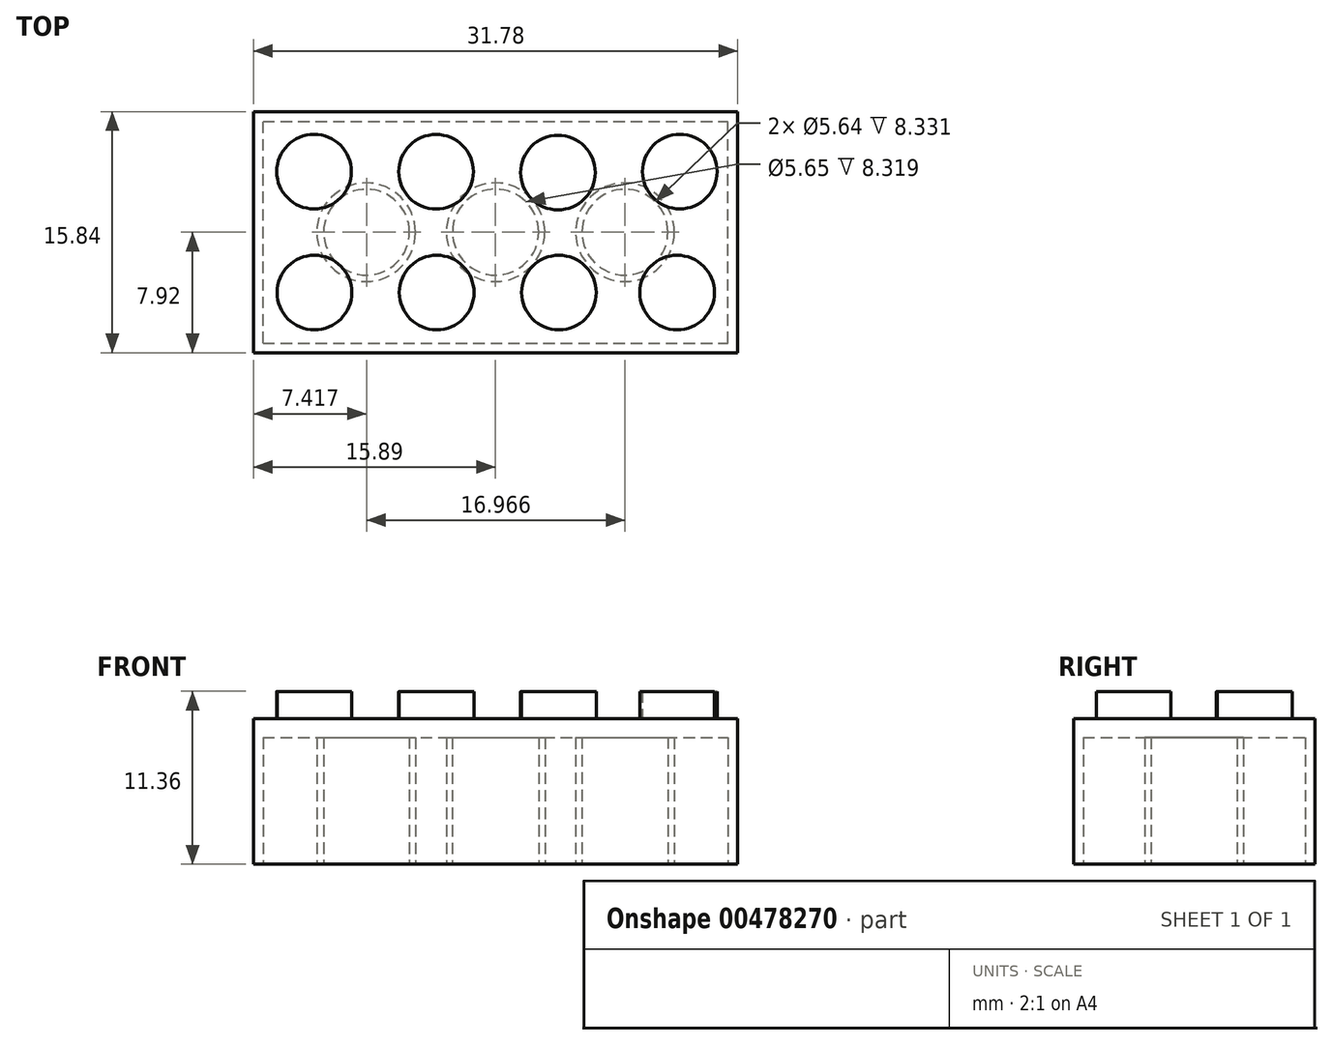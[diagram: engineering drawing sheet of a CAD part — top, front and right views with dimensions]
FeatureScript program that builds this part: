
annotation { "Feature Type Name" : "Feature", "Feature Type Description" : "" }
export const myFeature = defineFeature(function(context is Context, id is Id, definition is map)
    precondition{}
    {
        {
            var Q0;
            Q0=qCreatedBy(makeId("Top.planeOp"),FACE);
            var sketch = newSketch(context, id + "F0", { "sketchPlane" : qUnion([Q0])});
            skLineSegment(sketch, "E0.bottom", {"start": v(-15.9, 7.92) * mm, "end": v(15.9, 7.92) * mm});
            skLineSegment(sketch, "E0.top", {"start": v(-15.9, -7.92) * mm, "end": v(15.9, -7.92) * mm});
            skLineSegment(sketch, "E0.left", {"start": v(-15.9, 7.92) * mm, "end": v(-15.9, -7.92) * mm});
            skLineSegment(sketch, "E0.right", {"start": v(15.9, 7.92) * mm, "end": v(15.9, -7.92) * mm});
            skPoint(sketch, "E0.middle", {"position": v(0, 0) * mm});
            skSolve(sketch);
        }
        {
            var Q0;
            Q0=makeQuery(id+"F0.imprint","IMPRINT",FACE,{"disambiguationData":[TD([[makeQuery(id+"F0.imprint","IMPRINT",EDGE,{"derivedFrom":sQuery(id+"F0.wireOp",EDGE,"E0.bottom")}),-1.0]])]});
            extrude(context, id + "F1", {"entities" : qUnion([Q0]), "endBound" : BoundingType.SYMMETRIC, "depth" : 9.58 * mm, "offsetDistance" : 25.4 * mm});
        }
        {
            var Q0;
            Q0=makeQuery(id+"F1.opExtrude","CAP_FACE",FACE,{"disambiguationData":[OSD([sQuery(id+"F0.wireOp",EDGE,"E0.bottom"),sQuery(id+"F0.wireOp",EDGE,"E0.top"),sQuery(id+"F0.wireOp",EDGE,"E0.left"),sQuery(id+"F0.wireOp",EDGE,"E0.right")])],"isStart":false});
            var sketch = newSketch(context, id + "F2", { "sketchPlane" : qUnion([Q0])});
            skCircle(sketch, "E1", {"center": v(-11.92, 3.98) * mm, "radius": 2.45 * mm});
            skCircle(sketch, "E2", {"center": v(-11.92, -3.98) * mm, "radius": 2.45 * mm});
            skSolve(sketch);
        }
        {
            var Q0;
            Q0=makeQuery(id+"F2.imprint","IMPRINT",FACE,{"disambiguationData":[TD([[makeQuery(id+"F2.imprint","IMPRINT",EDGE,{"derivedFrom":sQuery(id+"F2.wireOp",EDGE,"E1")}),1.0]])]});
            extrude(context, id + "F3", {"entities" : qUnion([Q0]), "operationType" : NewBodyOperationType.ADD, "depth" : 1.78 * mm});
        }
        {
            var Q0;
            Q0=makeQuery(id+"F1.opExtrude","CAP_FACE",FACE,{"disambiguationData":[OSD([sQuery(id+"F0.wireOp",EDGE,"E0.bottom"),sQuery(id+"F0.wireOp",EDGE,"E0.top"),sQuery(id+"F0.wireOp",EDGE,"E0.left"),sQuery(id+"F0.wireOp",EDGE,"E0.right")])],"isStart":false});
            var sketch = newSketch(context, id + "F4", { "sketchPlane" : qUnion([Q0])});
            skCircle(sketch, "E3", {"center": v(-3.9, 3.97) * mm, "radius": 2.45 * mm});
            skSolve(sketch);
        }
        {
            var Q0;
            Q0=makeQuery(id+"F4.imprint","IMPRINT",FACE,{"disambiguationData":[TD([[makeQuery(id+"F4.imprint","IMPRINT",EDGE,{"derivedFrom":sQuery(id+"F4.wireOp",EDGE,"E3")}),1.0]])]});
            extrude(context, id + "F5", {"entities" : qUnion([Q0]), "operationType" : NewBodyOperationType.ADD, "depth" : 1.78 * mm});
        }
        {
            var Q0;
            Q0=makeQuery(id+"F1.opExtrude","CAP_FACE",FACE,{"disambiguationData":[OSD([sQuery(id+"F0.wireOp",EDGE,"E0.bottom"),sQuery(id+"F0.wireOp",EDGE,"E0.top"),sQuery(id+"F0.wireOp",EDGE,"E0.left"),sQuery(id+"F0.wireOp",EDGE,"E0.right")])],"isStart":false});
            var sketch = newSketch(context, id + "F6", { "sketchPlane" : qUnion([Q0])});
            skCircle(sketch, "E4", {"center": v(4.1, 3.92) * mm, "radius": 2.45 * mm});
            skSolve(sketch);
        }
        {
            var Q0;
            Q0=makeQuery(id+"F6.imprint","IMPRINT",FACE,{"disambiguationData":[TD([[makeQuery(id+"F6.imprint","IMPRINT",EDGE,{"derivedFrom":sQuery(id+"F6.wireOp",EDGE,"E4")}),1.0]])]});
            extrude(context, id + "F7", {"entities" : qUnion([Q0]), "operationType" : NewBodyOperationType.ADD, "depth" : 1.78 * mm});
        }
        {
            var Q0;
            Q0=makeQuery(id+"F1.opExtrude","CAP_FACE",FACE,{"disambiguationData":[OSD([sQuery(id+"F0.wireOp",EDGE,"E0.bottom"),sQuery(id+"F0.wireOp",EDGE,"E0.top"),sQuery(id+"F0.wireOp",EDGE,"E0.left"),sQuery(id+"F0.wireOp",EDGE,"E0.right")])],"isStart":false});
            var sketch = newSketch(context, id + "F8", { "sketchPlane" : qUnion([Q0])});
            skCircle(sketch, "E5", {"center": v(12.1, 3.98) * mm, "radius": 2.45 * mm});
            skSolve(sketch);
        }
        {
            var Q0;
            Q0=makeQuery(id+"F8.imprint","IMPRINT",FACE,{"disambiguationData":[TD([[makeQuery(id+"F8.imprint","IMPRINT",EDGE,{"derivedFrom":sQuery(id+"F8.wireOp",EDGE,"E5")}),1.0]])]});
            extrude(context, id + "F9", {"entities" : qUnion([Q0]), "operationType" : NewBodyOperationType.ADD, "depth" : 1.78 * mm});
        }
        {
            var Q0;
            Q0=makeQuery(id+"F1.opExtrude","CAP_FACE",FACE,{"disambiguationData":[OSD([sQuery(id+"F0.wireOp",EDGE,"E0.bottom"),sQuery(id+"F0.wireOp",EDGE,"E0.top"),sQuery(id+"F0.wireOp",EDGE,"E0.left"),sQuery(id+"F0.wireOp",EDGE,"E0.right")])],"isStart":false});
            var sketch = newSketch(context, id + "F10", { "sketchPlane" : qUnion([Q0])});
            skCircle(sketch, "E6", {"center": v(-11.9, -3.97) * mm, "radius": 2.45 * mm});
            skSolve(sketch);
        }
        {
            var Q0;
            Q0=makeQuery(id+"F10.imprint","IMPRINT",FACE,{"disambiguationData":[TD([[makeQuery(id+"F10.imprint","IMPRINT",EDGE,{"derivedFrom":sQuery(id+"F10.wireOp",EDGE,"E6")}),1.0]])]});
            extrude(context, id + "F11", {"entities" : qUnion([Q0]), "operationType" : NewBodyOperationType.ADD, "depth" : 1.78 * mm});
        }
        {
            var Q0;
            Q0=makeQuery(id+"F1.opExtrude","CAP_FACE",FACE,{"disambiguationData":[OSD([sQuery(id+"F0.wireOp",EDGE,"E0.bottom"),sQuery(id+"F0.wireOp",EDGE,"E0.top"),sQuery(id+"F0.wireOp",EDGE,"E0.left"),sQuery(id+"F0.wireOp",EDGE,"E0.right")])],"isStart":false});
            var sketch = newSketch(context, id + "F12", { "sketchPlane" : qUnion([Q0])});
            skCircle(sketch, "E7", {"center": v(-3.87, -3.97) * mm, "radius": 2.45 * mm});
            skSolve(sketch);
        }
        {
            var Q0;
            Q0=makeQuery(id+"F12.imprint","IMPRINT",FACE,{"disambiguationData":[TD([[makeQuery(id+"F12.imprint","IMPRINT",EDGE,{"derivedFrom":sQuery(id+"F12.wireOp",EDGE,"E7")}),1.0]])]});
            extrude(context, id + "F13", {"entities" : qUnion([Q0]), "operationType" : NewBodyOperationType.ADD, "depth" : 1.78 * mm});
        }
        {
            var Q0;
            Q0=makeQuery(id+"F1.opExtrude","CAP_FACE",FACE,{"disambiguationData":[OSD([sQuery(id+"F0.wireOp",EDGE,"E0.bottom"),sQuery(id+"F0.wireOp",EDGE,"E0.top"),sQuery(id+"F0.wireOp",EDGE,"E0.left"),sQuery(id+"F0.wireOp",EDGE,"E0.right")])],"isStart":false});
            var sketch = newSketch(context, id + "F14", { "sketchPlane" : qUnion([Q0])});
            skCircle(sketch, "E8", {"center": v(4.16, -3.97) * mm, "radius": 2.45 * mm});
            skSolve(sketch);
        }
        {
            var Q0;
            Q0=makeQuery(id+"F14.imprint","IMPRINT",FACE,{"disambiguationData":[TD([[makeQuery(id+"F14.imprint","IMPRINT",EDGE,{"derivedFrom":sQuery(id+"F14.wireOp",EDGE,"E8")}),1.0]])]});
            extrude(context, id + "F15", {"entities" : qUnion([Q0]), "operationType" : NewBodyOperationType.ADD, "depth" : 1.78 * mm});
        }
        {
            var Q0;
            Q0=makeQuery(id+"F1.opExtrude","CAP_FACE",FACE,{"disambiguationData":[OSD([sQuery(id+"F0.wireOp",EDGE,"E0.bottom"),sQuery(id+"F0.wireOp",EDGE,"E0.top"),sQuery(id+"F0.wireOp",EDGE,"E0.left"),sQuery(id+"F0.wireOp",EDGE,"E0.right")])],"isStart":false});
            var sketch = newSketch(context, id + "F16", { "sketchPlane" : qUnion([Q0])});
            skCircle(sketch, "E9", {"center": v(11.92, -3.97) * mm, "radius": 2.45 * mm});
            skSolve(sketch);
        }
        {
            var Q0;
            Q0=makeQuery(id+"F16.imprint","IMPRINT",FACE,{"disambiguationData":[TD([[makeQuery(id+"F16.imprint","IMPRINT",EDGE,{"derivedFrom":sQuery(id+"F16.wireOp",EDGE,"E9")}),1.0]])]});
            extrude(context, id + "F17", {"entities" : qUnion([Q0]), "operationType" : NewBodyOperationType.ADD, "depth" : 1.78 * mm});
        }
        {
            var Q0;
            Q0=makeQuery(id+"F1.opExtrude","CAP_FACE",FACE,{"disambiguationData":[OSD([sQuery(id+"F0.wireOp",EDGE,"E0.bottom"),sQuery(id+"F0.wireOp",EDGE,"E0.top"),sQuery(id+"F0.wireOp",EDGE,"E0.left"),sQuery(id+"F0.wireOp",EDGE,"E0.right")])],"isStart":true});
            var sketch = newSketch(context, id + "F18", { "sketchPlane" : qUnion([Q0])});
            skLineSegment(sketch, "E10.bottom", {"start": v(-15.27, 7.29) * mm, "end": v(15.27, 7.29) * mm});
            skLineSegment(sketch, "E10.top", {"start": v(-15.27, -7.29) * mm, "end": v(15.27, -7.29) * mm});
            skLineSegment(sketch, "E10.left", {"start": v(-15.27, 7.29) * mm, "end": v(-15.27, -7.29) * mm});
            skLineSegment(sketch, "E10.right", {"start": v(15.27, 7.29) * mm, "end": v(15.27, -7.29) * mm});
            skPoint(sketch, "E10.middle", {"position": v(0, 0) * mm});
            skSolve(sketch);
        }
        {
            var Q0;
            Q0=makeQuery(id+"F18.imprint","IMPRINT",FACE,{"disambiguationData":[TD([[makeQuery(id+"F18.imprint","IMPRINT",EDGE,{"derivedFrom":sQuery(id+"F18.wireOp",EDGE,"E10.bottom")}),-1.0]])]});
            var sketch = newSketch(context, id + "F19", { "sketchPlane" : qUnion([Q0])});
            skCircle(sketch, "E11", {"center": v(0, 0) * mm, "radius": 3.24 * mm});
            skSolve(sketch);
        }
        {
            var Q0;
            Q0=makeQuery(id+"F19.imprint","IMPRINT",FACE,{"disambiguationData":[TD([[makeQuery(id+"F19.imprint","IMPRINT",EDGE,{"derivedFrom":sQuery(id+"F19.wireOp",EDGE,"E11")}),-1.0]])]});
            var sketch = newSketch(context, id + "F20", { "sketchPlane" : qUnion([Q0])});
            skCircle(sketch, "E12", {"center": v(0, 0) * mm, "radius": 2.83 * mm});
            skSolve(sketch);
        }
        {
            var Q0;
            Q0 = qSketchRegion(id + "F19", true);
            var Q1;
            Q1=sQuery(id+"F19.wireOp",EDGE,"E11");
            extrude(context, id + "F21", {"entities" : qUnion([Q0]), "bodyType" : ToolBodyType.SURFACE, "operationType" : NewBodyOperationType.REMOVE, "surfaceEntities" : qUnion([Q1]), "oppositeDirection" : true, "depth" : 8.32 * mm, "offsetDistance" : 25.4 * mm});
        }
        {
            var Q0;
            Q0 = qSketchRegion(id + "F20", true);
            extrude(context, id + "F22", {"entities" : qUnion([Q0]), "operationType" : NewBodyOperationType.REMOVE, "oppositeDirection" : true, "depth" : 8.32 * mm, "offsetDistance" : 25.4 * mm});
        }
        {
            var Q0;
            Q0=makeQuery(id+"F20.imprint","IMPRINT",FACE,{"disambiguationData":[TD([[makeQuery(id+"F20.imprint","IMPRINT",EDGE,{"derivedFrom":makeQuery(id+"F19.imprint","IMPRINT",EDGE,{"derivedFrom":sQuery(id+"F19.wireOp",EDGE,"E11")})}),-1.0]])]});
            extrude(context, id + "F23", {"entities" : qUnion([Q0]), "operationType" : NewBodyOperationType.REMOVE, "oppositeDirection" : true, "depth" : 8.32 * mm, "offsetDistance" : 25.4 * mm});
        }
        {
            var Q0;
            Q0=makeQuery(id+"F20.imprint","IMPRINT",FACE,{"disambiguationData":[TD([[makeQuery(id+"F20.imprint","IMPRINT",EDGE,{"derivedFrom":makeQuery(id+"F19.imprint","IMPRINT",EDGE,{"derivedFrom":sQuery(id+"F19.wireOp",EDGE,"E11")})}),-1.0]])]});
            var sketch = newSketch(context, id + "F24", { "sketchPlane" : qUnion([Q0])});
            skCircle(sketch, "E13", {"center": v(-8.5, 0) * mm, "radius": 3.24 * mm});
            skSolve(sketch);
        }
        {
            var Q0;
            Q0=makeQuery(id+"F20.imprint","IMPRINT",FACE,{"disambiguationData":[TD([[makeQuery(id+"F20.imprint","IMPRINT",EDGE,{"derivedFrom":makeQuery(id+"F19.imprint","IMPRINT",EDGE,{"derivedFrom":sQuery(id+"F19.wireOp",EDGE,"E11")})}),-1.0]])]});
            var sketch = newSketch(context, id + "F25", { "sketchPlane" : qUnion([Q0])});
            skCircle(sketch, "E14", {"center": v(8.5, 0) * mm, "radius": 3.24 * mm});
            skSolve(sketch);
        }
        {
            var Q0;
            Q0=makeQuery(id+"F20.imprint","IMPRINT",FACE,{"disambiguationData":[TD([[makeQuery(id+"F20.imprint","IMPRINT",EDGE,{"derivedFrom":makeQuery(id+"F19.imprint","IMPRINT",EDGE,{"derivedFrom":sQuery(id+"F19.wireOp",EDGE,"E11")})}),-1.0]])]});
            var sketch = newSketch(context, id + "F26", { "sketchPlane" : qUnion([Q0])});
            skCircle(sketch, "E15", {"center": v(-8.47, 0) * mm, "radius": 2.82 * mm});
            skSolve(sketch);
        }
        {
            var Q0;
            Q0=makeQuery(id+"F20.imprint","IMPRINT",FACE,{"disambiguationData":[TD([[makeQuery(id+"F20.imprint","IMPRINT",EDGE,{"derivedFrom":makeQuery(id+"F19.imprint","IMPRINT",EDGE,{"derivedFrom":sQuery(id+"F19.wireOp",EDGE,"E11")})}),-1.0]])]});
            var sketch = newSketch(context, id + "F27", { "sketchPlane" : qUnion([Q0])});
            skCircle(sketch, "E16", {"center": v(8.5, 0) * mm, "radius": 2.82 * mm});
            skSolve(sketch);
        }
        {
            var Q0;
            Q0 = qSketchRegion(id + "F24", true);
            extrude(context, id + "F28", {"entities" : qUnion([Q0]), "operationType" : NewBodyOperationType.ADD, "oppositeDirection" : true, "depth" : 8.33 * mm, "offsetDistance" : 25.4 * mm});
        }
        {
            var Q0;
            Q0 = qSketchRegion(id + "F25", true);
            extrude(context, id + "F29", {"entities" : qUnion([Q0]), "operationType" : NewBodyOperationType.ADD, "oppositeDirection" : true, "depth" : 8.33 * mm, "offsetDistance" : 25.4 * mm});
        }
        {
            var Q0;
            Q0 = qSketchRegion(id + "F26", true);
            extrude(context, id + "F30", {"entities" : qUnion([Q0]), "operationType" : NewBodyOperationType.REMOVE, "oppositeDirection" : true, "depth" : 8.33 * mm, "offsetDistance" : 25.4 * mm});
        }
        {
            var Q0;
            Q0 = qSketchRegion(id + "F27", true);
            extrude(context, id + "F31", {"entities" : qUnion([Q0]), "operationType" : NewBodyOperationType.REMOVE, "oppositeDirection" : true, "depth" : 8.33 * mm, "offsetDistance" : 25.4 * mm});
        }
    });
